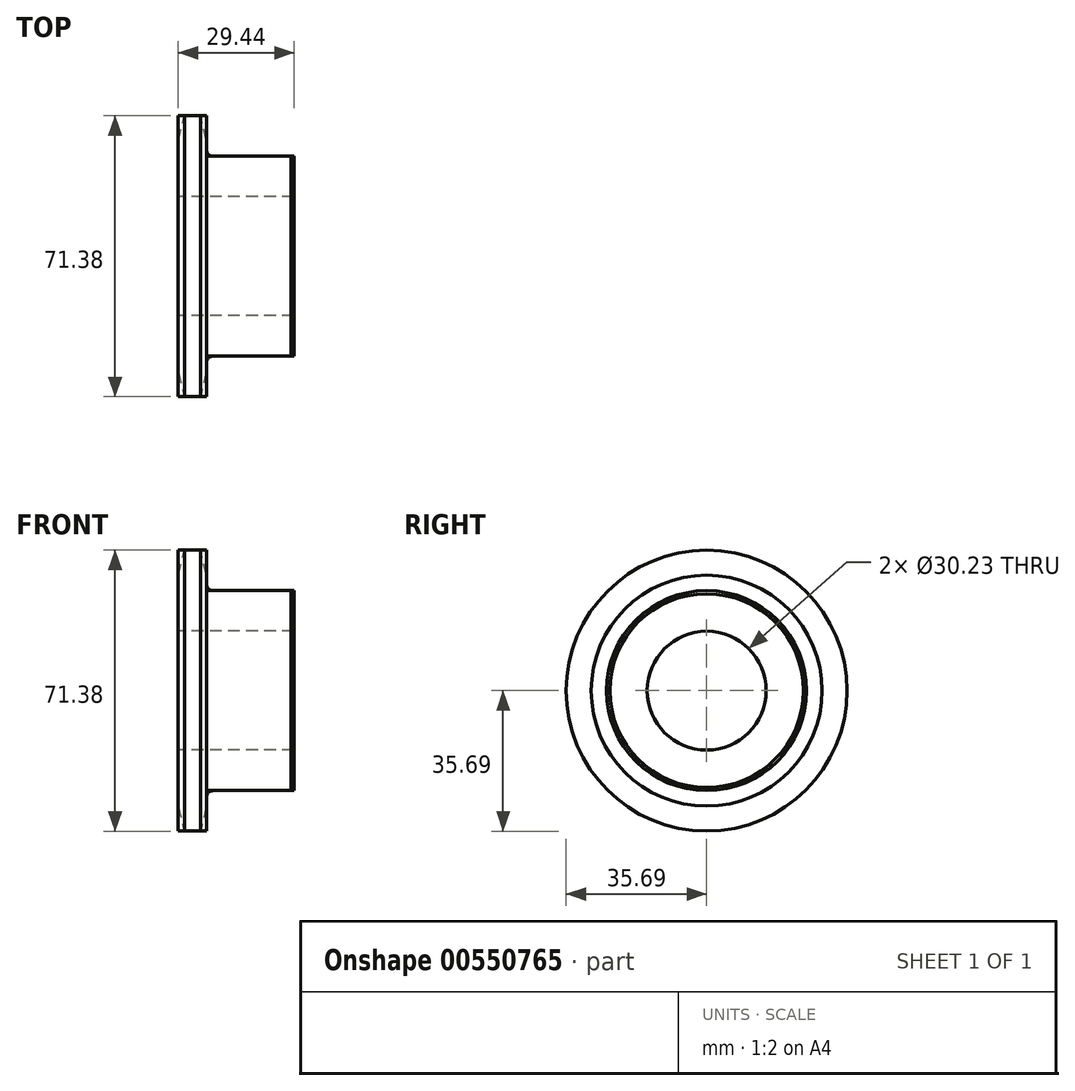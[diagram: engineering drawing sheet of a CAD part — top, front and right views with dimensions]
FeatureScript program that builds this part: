
annotation { "Feature Type Name" : "Feature", "Feature Type Description" : "" }
export const myFeature = defineFeature(function(context is Context, id is Id, definition is map)
    precondition{}
    {
        {
            var Q0;
            Q0=qCreatedBy(makeId("Front.planeOp"),FACE);
            var sketch = newSketch(context, id + "F0", { "sketchPlane" : qUnion([Q0])});
            skLineSegment(sketch, "E0", {"start": v(-29.44, 0) * mm, "end": v(0, 0) * mm});
            skLineSegment(sketch, "E1.bottom", {"start": v(-29.44, 35.69) * mm, "end": v(-22.23, 35.69) * mm});
            skLineSegment(sketch, "E1.top", {"start": v(-29.44, 15.11) * mm, "end": v(-22.23, 15.11) * mm});
            skLineSegment(sketch, "E1.left", {"start": v(-22.23, 35.69) * mm, "end": v(-22.23, 15.11) * mm});
            skLineSegment(sketch, "E1.right", {"start": v(-29.44, 35.69) * mm, "end": v(-29.44, 15.11) * mm});
            skLineSegment(sketch, "E2.bottom", {"start": v(-22.22, 25.4) * mm, "end": v(0, 25.4) * mm});
            skLineSegment(sketch, "E2.top", {"start": v(-22.23, 15.11) * mm, "end": v(0, 15.11) * mm});
            skLineSegment(sketch, "E2.left", {"start": v(-22.23, 25.4) * mm, "end": v(-22.23, 15.11) * mm});
            skLineSegment(sketch, "E2.right", {"start": v(0, 25.4) * mm, "end": v(0, 15.11) * mm});
            skLineSegment(sketch, "E3.MirrorCS", {"start": v(-22.22, -35.69) * mm, "end": v(-22.22, -15.11) * mm});
            skLineSegment(sketch, "E4.MirrorCS", {"start": v(-22.22, -25.4) * mm, "end": v(0, -25.4) * mm});
            skLineSegment(sketch, "E5.MirrorCS", {"start": v(-29.44, -15.11) * mm, "end": v(-22.23, -15.11) * mm});
            skLineSegment(sketch, "E6.MirrorCS", {"start": v(-29.44, -35.69) * mm, "end": v(-22.23, -35.69) * mm});
            skLineSegment(sketch, "E7.MirrorCS", {"start": v(-22.23, -15.11) * mm, "end": v(0, -15.11) * mm});
            skLineSegment(sketch, "E8.MirrorCS", {"start": v(-29.44, -35.69) * mm, "end": v(-29.44, -15.11) * mm});
            skLineSegment(sketch, "E9.MirrorCS", {"start": v(-22.22, -25.4) * mm, "end": v(-22.23, -15.11) * mm});
            skLineSegment(sketch, "E10.MirrorCS", {"start": v(0, -25.4) * mm, "end": v(0, -15.11) * mm});
            skSolve(sketch);
        }
        {
            var Q0;
            Q0 = qSketchRegion(id + "F0", true);
            var Q1;
            Q1=sQuery(id+"F0.wireOp",EDGE,"E0");
            revolve(context, id + "F1", {"entities" : qUnion([Q0]), "axis" : qUnion([Q1]), "revolveType" : RevolveType.FULL});
        }
        {
            var Q0;
            Q0=makeQuery(id+"F1.opRevolve","SWEPT_EDGE",EDGE,{"disambiguationData":[OSD([sQuery(id+"F0.wireOp",EDGE,"E1.left"),sQuery(id+"F0.wireOp",EDGE,"E2.bottom"),sQuery(id+"F0.wireOp",EDGE,"E2.left")])]});
            fillet(context, id + "F2", {"entities" : qUnion([Q0]), "radius" : 1.59 * mm, "tangentPropagation" : true, "allowEdgeOverflow" : false});
        }
        {
            var Q0;
            Q0=makeQuery(id+"F1.opRevolve","SWEPT_EDGE",EDGE,{"disambiguationData":[OSD([sQuery(id+"F0.wireOp",EDGE,"E2.bottom"),sQuery(id+"F0.wireOp",EDGE,"E2.right")])]});
            chamfer(context, id + "F3", {"entities" : qUnion([Q0]), "width" : 0.8 * mm, "tangentPropagation" : true});
        }
        {
            var Q0;
            Q0=makeQuery(id+"F1.opRevolve","SWEPT_FACE",FACE,{"disambiguationData":[OSD([sQuery(id+"F0.wireOp",EDGE,"E1.bottom")])]});
            chamfer(context, id + "F4", {"entities" : qUnion([Q0]), "chamferType" : ChamferType.TWO_OFFSETS, "width1" : 6.35 * mm, "oppositeDirection" : false, "width2" : 1.57 * mm, "tangentPropagation" : true});
        }
    });
